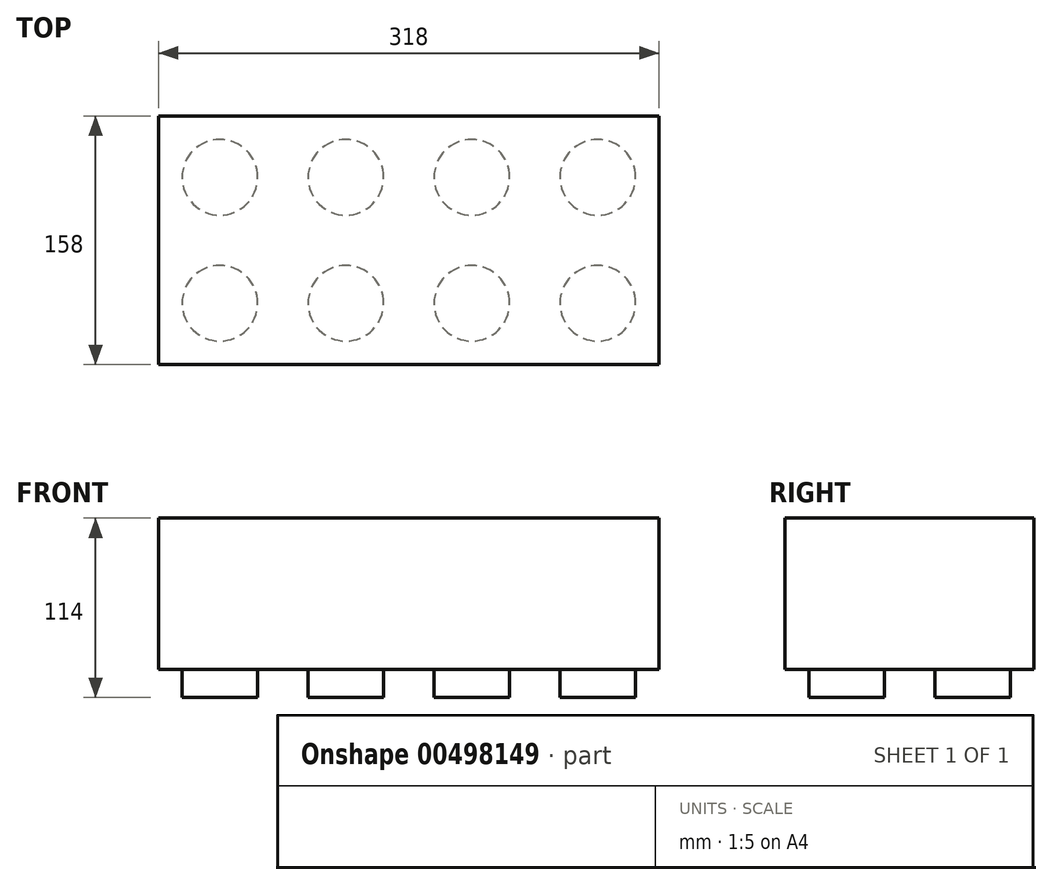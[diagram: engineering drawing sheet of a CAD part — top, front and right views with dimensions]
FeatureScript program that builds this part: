
annotation { "Feature Type Name" : "Feature", "Feature Type Description" : "" }
export const myFeature = defineFeature(function(context is Context, id is Id, definition is map)
    precondition{}
    {
        {
            var Q0;
            Q0=qCreatedBy(makeId("Top.planeOp"),FACE);
            var sketch = newSketch(context, id + "F0", { "sketchPlane" : qUnion([Q0])});
            skLineSegment(sketch, "E0.bottom", {"start": v(0, 0) * mm, "end": v(318, 0) * mm});
            skLineSegment(sketch, "E0.top", {"start": v(0, 158) * mm, "end": v(318, 158) * mm});
            skLineSegment(sketch, "E0.left", {"start": v(0, 0) * mm, "end": v(0, 158) * mm});
            skLineSegment(sketch, "E0.right", {"start": v(318, 0) * mm, "end": v(318, 158) * mm});
            skCircle(sketch, "E1", {"center": v(39, 119) * mm, "radius": 24 * mm});
            skCircle(sketch, "E2", {"center": v(119, 119) * mm, "radius": 24 * mm});
            skCircle(sketch, "E3", {"center": v(199, 119) * mm, "radius": 24 * mm});
            skCircle(sketch, "E4", {"center": v(279, 119) * mm, "radius": 24 * mm});
            skCircle(sketch, "E5", {"center": v(39, 39) * mm, "radius": 24 * mm});
            skCircle(sketch, "E6", {"center": v(119, 39) * mm, "radius": 24 * mm});
            skCircle(sketch, "E7", {"center": v(199, 39) * mm, "radius": 24 * mm});
            skCircle(sketch, "E8", {"center": v(279, 39) * mm, "radius": 24 * mm});
            skSolve(sketch);
        }
        {
            var Q0;
            Q0=makeQuery(id+"F0.imprint","IMPRINT",FACE,{"disambiguationData":[TD([[makeQuery(id+"F0.imprint","IMPRINT",EDGE,{"derivedFrom":sQuery(id+"F0.wireOp",EDGE,"E5")}),1.0]])]});
            var Q1;
            Q1=makeQuery(id+"F0.imprint","IMPRINT",FACE,{"disambiguationData":[TD([[makeQuery(id+"F0.imprint","IMPRINT",EDGE,{"derivedFrom":sQuery(id+"F0.wireOp",EDGE,"E1")}),1.0]])]});
            var Q2;
            Q2=makeQuery(id+"F0.imprint","IMPRINT",FACE,{"disambiguationData":[TD([[makeQuery(id+"F0.imprint","IMPRINT",EDGE,{"derivedFrom":sQuery(id+"F0.wireOp",EDGE,"E2")}),1.0]])]});
            var Q3;
            Q3=makeQuery(id+"F0.imprint","IMPRINT",FACE,{"disambiguationData":[TD([[makeQuery(id+"F0.imprint","IMPRINT",EDGE,{"derivedFrom":sQuery(id+"F0.wireOp",EDGE,"E6")}),1.0]])]});
            var Q4;
            Q4=makeQuery(id+"F0.imprint","IMPRINT",FACE,{"disambiguationData":[TD([[makeQuery(id+"F0.imprint","IMPRINT",EDGE,{"derivedFrom":sQuery(id+"F0.wireOp",EDGE,"E3")}),1.0]])]});
            var Q5;
            Q5=makeQuery(id+"F0.imprint","IMPRINT",FACE,{"disambiguationData":[TD([[makeQuery(id+"F0.imprint","IMPRINT",EDGE,{"derivedFrom":sQuery(id+"F0.wireOp",EDGE,"E7")}),1.0]])]});
            var Q6;
            Q6=makeQuery(id+"F0.imprint","IMPRINT",FACE,{"disambiguationData":[TD([[makeQuery(id+"F0.imprint","IMPRINT",EDGE,{"derivedFrom":sQuery(id+"F0.wireOp",EDGE,"E8")}),1.0]])]});
            var Q7;
            Q7=makeQuery(id+"F0.imprint","IMPRINT",FACE,{"disambiguationData":[TD([[makeQuery(id+"F0.imprint","IMPRINT",EDGE,{"derivedFrom":sQuery(id+"F0.wireOp",EDGE,"E4")}),1.0]])]});
            var Q8;
            Q8=makeQuery(id+"F0.imprint","IMPRINT",FACE,{"disambiguationData":[TD([[makeQuery(id+"F0.imprint","IMPRINT",EDGE,{"derivedFrom":sQuery(id+"F0.wireOp",EDGE,"E0.bottom")}),1.0]])]});
            extrude(context, id + "F1", {"entities" : qUnion([Q0, Q1, Q2, Q3, Q4, Q5, Q6, Q7, Q8]), "depth" : 96 * mm});
        }
        {
            var Q0;
            Q0=makeQuery(id+"F0.imprint","IMPRINT",FACE,{"disambiguationData":[TD([[makeQuery(id+"F0.imprint","IMPRINT",EDGE,{"derivedFrom":sQuery(id+"F0.wireOp",EDGE,"E5")}),1.0]])]});
            var Q1;
            Q1=makeQuery(id+"F0.imprint","IMPRINT",FACE,{"disambiguationData":[TD([[makeQuery(id+"F0.imprint","IMPRINT",EDGE,{"derivedFrom":sQuery(id+"F0.wireOp",EDGE,"E1")}),1.0]])]});
            var Q2;
            Q2=makeQuery(id+"F0.imprint","IMPRINT",FACE,{"disambiguationData":[TD([[makeQuery(id+"F0.imprint","IMPRINT",EDGE,{"derivedFrom":sQuery(id+"F0.wireOp",EDGE,"E2")}),1.0]])]});
            var Q3;
            Q3=makeQuery(id+"F0.imprint","IMPRINT",FACE,{"disambiguationData":[TD([[makeQuery(id+"F0.imprint","IMPRINT",EDGE,{"derivedFrom":sQuery(id+"F0.wireOp",EDGE,"E6")}),1.0]])]});
            var Q4;
            Q4=makeQuery(id+"F0.imprint","IMPRINT",FACE,{"disambiguationData":[TD([[makeQuery(id+"F0.imprint","IMPRINT",EDGE,{"derivedFrom":sQuery(id+"F0.wireOp",EDGE,"E7")}),1.0]])]});
            var Q5;
            Q5=makeQuery(id+"F0.imprint","IMPRINT",FACE,{"disambiguationData":[TD([[makeQuery(id+"F0.imprint","IMPRINT",EDGE,{"derivedFrom":sQuery(id+"F0.wireOp",EDGE,"E3")}),1.0]])]});
            var Q6;
            Q6=makeQuery(id+"F0.imprint","IMPRINT",FACE,{"disambiguationData":[TD([[makeQuery(id+"F0.imprint","IMPRINT",EDGE,{"derivedFrom":sQuery(id+"F0.wireOp",EDGE,"E4")}),1.0]])]});
            var Q7;
            Q7=makeQuery(id+"F0.imprint","IMPRINT",FACE,{"disambiguationData":[TD([[makeQuery(id+"F0.imprint","IMPRINT",EDGE,{"derivedFrom":sQuery(id+"F0.wireOp",EDGE,"E8")}),1.0]])]});
            var Q8;
            Q8=sQuery(id+"F0.wireOp",EDGE,"E8");
            var Q9;
            Q9=sQuery(id+"F0.wireOp",EDGE,"E4");
            var Q10;
            Q10=sQuery(id+"F0.wireOp",EDGE,"E7");
            var Q11;
            Q11=sQuery(id+"F0.wireOp",EDGE,"E3");
            var Q12;
            Q12=sQuery(id+"F0.wireOp",EDGE,"E6");
            var Q13;
            Q13=sQuery(id+"F0.wireOp",EDGE,"E2");
            var Q14;
            Q14=sQuery(id+"F0.wireOp",EDGE,"E5");
            var Q15;
            Q15=sQuery(id+"F0.wireOp",EDGE,"E1");
            extrude(context, id + "F2", {"entities" : qUnion([Q0, Q1, Q2, Q3, Q4, Q5, Q6, Q7]), "operationType" : NewBodyOperationType.ADD, "surfaceEntities" : qUnion([Q8, Q9, Q10, Q11, Q12, Q13, Q14, Q15]), "oppositeDirection" : true, "depth" : 18 * mm});
        }
    });
